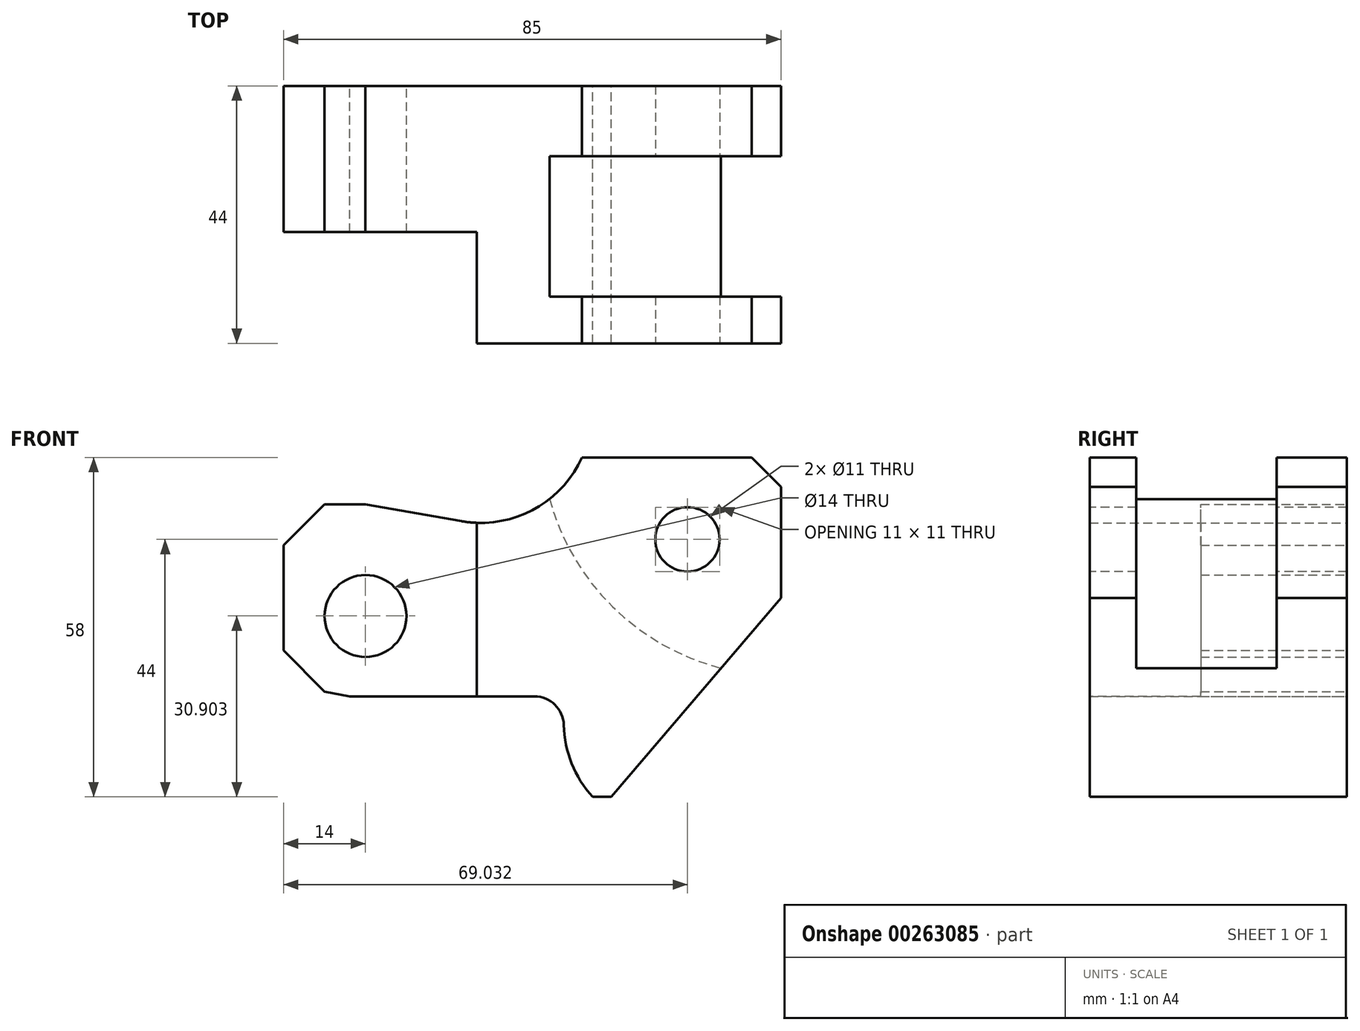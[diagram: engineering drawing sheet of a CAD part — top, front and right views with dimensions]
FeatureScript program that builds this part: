
annotation { "Feature Type Name" : "Feature", "Feature Type Description" : "" }
export const myFeature = defineFeature(function(context is Context, id is Id, definition is map)
    precondition{}
    {
        {
            var Q0;
            Q0=qCreatedBy(makeId("Front.planeOp"),FACE);
            var sketch = newSketch(context, id + "F0", { "sketchPlane" : qUnion([Q0])});
            skLineSegment(sketch, "E0", {"start": v(0, 0) * mm, "end": v(-29, -34) * mm});
            skLineSegment(sketch, "E1", {"start": v(-5, 24) * mm, "end": v(0, 19) * mm});
            skLineSegment(sketch, "E2", {"start": v(0, 19) * mm, "end": v(0, 0) * mm});
            skLineSegment(sketch, "E3", {"start": v(-34, 24) * mm, "end": v(-5, 24) * mm});
            skLineSegment(sketch, "E4", {"start": v(-78, 16) * mm, "end": v(-85, 9) * mm});
            skLineSegment(sketch, "E5", {"start": v(-78, 16) * mm, "end": v(-71, 16) * mm});
            skLineSegment(sketch, "E6", {"start": v(-85, 9) * mm, "end": v(-85, 0) * mm});
            skLineSegment(sketch, "E7", {"start": v(-78, -16) * mm, "end": v(-73.67, -16.84) * mm});
            skLineSegment(sketch, "E8", {"start": v(-85, 0) * mm, "end": v(-85, -9) * mm});
            skLineSegment(sketch, "E9", {"start": v(-78, -16) * mm, "end": v(-85, -9) * mm});
            skLineSegment(sketch, "E10", {"start": v(-71, 16) * mm, "end": v(-54.61, 13.11) * mm});
            skArc(sketch, "E11", {"start": v(-54.61, 13.11) * mm, "mid": v(-42.44, 15.02) * mm, "end": v(-34, 24) * mm});
            skLineSegment(sketch, "E12", {"start": v(-73.67, -16.84) * mm, "end": v(-71, -3.1) * mm});
            skCircle(sketch, "E13", {"center": v(-71, -3.1) * mm, "radius": 7 * mm});
            skLineSegment(sketch, "E14", {"start": v(-73.67, -16.84) * mm, "end": v(-42.11, -16.84) * mm});
            skLineSegment(sketch, "E15", {"start": v(-29, -34) * mm, "end": v(-32.2, -34) * mm});
            skArc(sketch, "E16", {"start": v(-37.11, -21.72) * mm, "mid": v(-35.76, -28.3) * mm, "end": v(-32.2, -34) * mm});
            skPoint(sketch, "E17.visualSharp", {"position": v(-36.6, -16.84) * mm});
            skArc(sketch, "E17.filletArc", {"start": v(-37.11, -21.72) * mm, "mid": v(-38.62, -18.26) * mm, "end": v(-42.11, -16.84) * mm});
            skSolve(sketch);
        }
        {
            var Q0;
            Q0=makeQuery(id+"F0.imprint","IMPRINT",FACE,{"disambiguationData":[TD([[makeQuery(id+"F0.imprint","IMPRINT",EDGE,{"derivedFrom":sQuery(id+"F0.wireOp",EDGE,"E0")}),-1.0]])]});
            extrude(context, id + "F1", {"entities" : qUnion([Q0]), "depth" : 44 * mm});
        }
        {
            var Q0;
            Q0=makeQuery(id+"F1.opExtrude","CAP_FACE",FACE,{"disambiguationData":[OSD([sQuery(id+"F0.wireOp",EDGE,"E0"),sQuery(id+"F0.wireOp",EDGE,"E1"),sQuery(id+"F0.wireOp",EDGE,"E2"),sQuery(id+"F0.wireOp",EDGE,"E3"),sQuery(id+"F0.wireOp",EDGE,"E4"),sQuery(id+"F0.wireOp",EDGE,"E5"),sQuery(id+"F0.wireOp",EDGE,"E6"),sQuery(id+"F0.wireOp",EDGE,"E7"),sQuery(id+"F0.wireOp",EDGE,"E8"),sQuery(id+"F0.wireOp",EDGE,"E9"),sQuery(id+"F0.wireOp",EDGE,"E10"),sQuery(id+"F0.wireOp",EDGE,"E11"),sQuery(id+"F0.wireOp",EDGE,"E13"),sQuery(id+"F0.wireOp",EDGE,"E14"),sQuery(id+"F0.wireOp",EDGE,"E15"),sQuery(id+"F0.wireOp",EDGE,"E16")])],"isStart":false});
            var sketch = newSketch(context, id + "F2", { "sketchPlane" : qUnion([Q0])});
            skCircle(sketch, "E18", {"center": v(-15.97, 10) * mm, "radius": 5.5 * mm});
            skSolve(sketch);
        }
        {
            var Q0;
            Q0=makeQuery(id+"F2.imprint","IMPRINT",FACE,{"disambiguationData":[TD([[makeQuery(id+"F2.imprint","IMPRINT",EDGE,{"derivedFrom":sQuery(id+"F2.wireOp",EDGE,"E18")}),1.0]])]});
            var Q1;
            Q1=sQuery(id+"F2.wireOp",EDGE,"E18");
            extrude(context, id + "F3", {"entities" : qUnion([Q0]), "operationType" : NewBodyOperationType.REMOVE, "surfaceEntities" : qUnion([Q1]), "endBound" : BoundingType.THROUGH_ALL, "oppositeDirection" : true, "depth" : 25 * mm});
        }
        {
            var Q0;
            Q0=qCreatedBy(makeId("Top.planeOp"),FACE);
            var sketch = newSketch(context, id + "F4", { "sketchPlane" : qUnion([Q0])});
            skPoint(sketch, "E19.0", {"position": v(-85, -44) * mm});
            skLineSegment(sketch, "E20.bottom", {"start": v(-85, -44) * mm, "end": v(-52, -44) * mm});
            skLineSegment(sketch, "E20.top", {"start": v(-85, -25) * mm, "end": v(-52, -25) * mm});
            skLineSegment(sketch, "E20.left", {"start": v(-85, -44) * mm, "end": v(-85, -25) * mm});
            skLineSegment(sketch, "E20.right", {"start": v(-52, -44) * mm, "end": v(-52, -25) * mm});
            skSolve(sketch);
        }
        {
            var Q0;
            Q0 = qSketchRegion(id + "F4", true);
            extrude(context, id + "F5", {"entities" : qUnion([Q0]), "operationType" : NewBodyOperationType.REMOVE, "endBound" : BoundingType.THROUGH_ALL, "depth" : 25 * mm, "hasSecondDirection" : true, "secondDirectionOppositeDirection" : true, "secondDirectionDepth" : 25 * mm});
        }
        {
            var Q0;
            Q0=makeQuery(id+"F1.opExtrude","CAP_FACE",FACE,{"disambiguationData":[OSD([sQuery(id+"F0.wireOp",EDGE,"E0"),sQuery(id+"F0.wireOp",EDGE,"E1"),sQuery(id+"F0.wireOp",EDGE,"E2"),sQuery(id+"F0.wireOp",EDGE,"E3"),sQuery(id+"F0.wireOp",EDGE,"E4"),sQuery(id+"F0.wireOp",EDGE,"E5"),sQuery(id+"F0.wireOp",EDGE,"E6"),sQuery(id+"F0.wireOp",EDGE,"E7"),sQuery(id+"F0.wireOp",EDGE,"E8"),sQuery(id+"F0.wireOp",EDGE,"E9"),sQuery(id+"F0.wireOp",EDGE,"E10"),sQuery(id+"F0.wireOp",EDGE,"E11"),sQuery(id+"F0.wireOp",EDGE,"E13"),sQuery(id+"F0.wireOp",EDGE,"E14"),sQuery(id+"F0.wireOp",EDGE,"E15"),sQuery(id+"F0.wireOp",EDGE,"E16"),sQuery(id+"F0.wireOp",EDGE,"E17.filletArc")])],"isStart":true});
            cPlane(context, id + "F6", {"entities" : qUnion([Q0]), "cplaneType" : CPlaneType.OFFSET, "offset" : 12 * mm, "oppositeDirection" : true, "width" : 150 * mm, "height" : 150 * mm});
        }
        {
            var Q0;
            Q0=qCreatedBy(id+"F6.planeOp",FACE);
            var sketch = newSketch(context, id + "F7", { "sketchPlane" : qUnion([Q0])});
            skArc(sketch, "E21", {"start": v(10.24, -12) * mm, "mid": v(28.78, -1.5) * mm, "end": v(39.55, 16.9) * mm});
            skArc(sketch, "E22.0", {"start": v(52, 12.83) * mm, "mid": v(41.3, 15.68) * mm, "end": v(34, 24) * mm});
            skLineSegment(sketch, "E23.0", {"start": v(34, 24) * mm, "end": v(5, 24) * mm});
            skArc(sketch, "E24.0.0", {"start": v(34, 24) * mm, "mid": v(41.3, 15.68) * mm, "end": v(52, 12.83) * mm});
            skLineSegment(sketch, "E24.0.1", {"start": v(52, 12.83) * mm, "end": v(52, -16.84) * mm});
            skLineSegment(sketch, "E24.0.2", {"start": v(52, -16.84) * mm, "end": v(42.11, -16.84) * mm});
            skArc(sketch, "E24.0.3", {"start": v(42.11, -16.84) * mm, "mid": v(38.62, -18.26) * mm, "end": v(37.11, -21.72) * mm});
            skArc(sketch, "E24.0.4", {"start": v(37.11, -21.72) * mm, "mid": v(35.76, -28.3) * mm, "end": v(32.2, -34) * mm});
            skLineSegment(sketch, "E24.0.5", {"start": v(32.2, -34) * mm, "end": v(29, -34) * mm});
            skLineSegment(sketch, "E24.0.6", {"start": v(29, -34) * mm, "end": v(0, 0) * mm});
            skLineSegment(sketch, "E24.0.7", {"start": v(0, 0) * mm, "end": v(0, 19) * mm});
            skLineSegment(sketch, "E24.0.8", {"start": v(0, 19) * mm, "end": v(5, 24) * mm});
            skLineSegment(sketch, "E24.0.9", {"start": v(5, 24) * mm, "end": v(34, 24) * mm});
            skSolve(sketch);
        }
        {
            var Q0;
            {var subQ1=sQuery(id+"F7.wireOp",EDGE,"E21");Q0=makeQuery(id+"F7.imprint","IMPRINT",FACE,{"disambiguationData":[TD([[makeQuery(id+"F7.imprint","IMPRINT",EDGE,{"derivedFrom":subQ1}),1.0]])]});}
            extrude(context, id + "F8", {"entities" : qUnion([Q0]), "operationType" : NewBodyOperationType.REMOVE, "oppositeDirection" : true, "depth" : 24 * mm});
        }
    });
